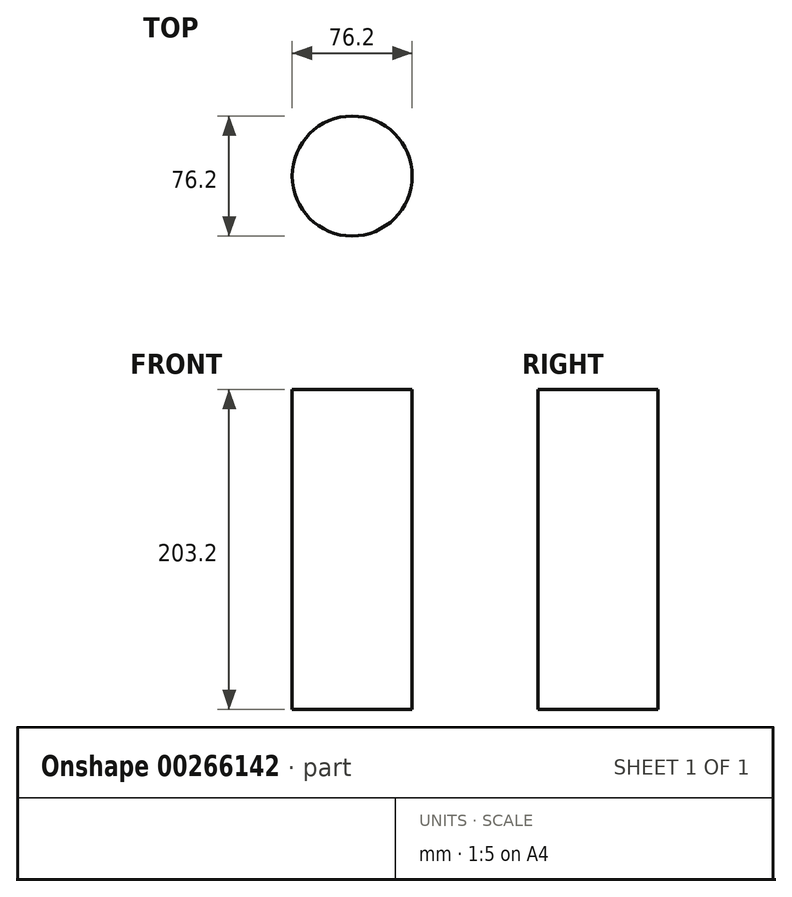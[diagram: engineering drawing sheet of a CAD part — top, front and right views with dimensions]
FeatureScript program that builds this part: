
annotation { "Feature Type Name" : "Feature", "Feature Type Description" : "" }
export const myFeature = defineFeature(function(context is Context, id is Id, definition is map)
    precondition{}
    {
        {
            var Q0;
            Q0=qCreatedBy(makeId("Front.planeOp"),FACE);
            var sketch = newSketch(context, id + "F0", { "sketchPlane" : qUnion([Q0])});
            skLineSegment(sketch, "E0.left", {"start": v(38.1, 101.6) * mm, "end": v(38.1, -101.6) * mm});
            skPoint(sketch, "E0.middle", {"position": v(0, 0) * mm});
            skLineSegment(sketch, "E1", {"start": v(0, 101.6) * mm, "end": v(0, -101.6) * mm});
            skLineSegment(sketch, "E2", {"start": v(0, 101.6) * mm, "end": v(38.1, 101.6) * mm});
            skLineSegment(sketch, "E3", {"start": v(0, -101.6) * mm, "end": v(38.1, -101.6) * mm});
            skSolve(sketch);
        }
        {
            var Q0;
            Q0=makeQuery(id+"F0.imprint","IMPRINT",FACE,{"disambiguationData":[TD([[makeQuery(id+"F0.imprint","IMPRINT",EDGE,{"derivedFrom":sQuery(id+"F0.wireOp",EDGE,"E0.left")}),-1.0]])]});
            var Q1;
            Q1=sQuery(id+"F0.wireOp",EDGE,"E1");
            revolve(context, id + "F1", {"entities" : qUnion([Q0]), "axis" : qUnion([Q1]), "revolveType" : RevolveType.FULL});
        }
    });
